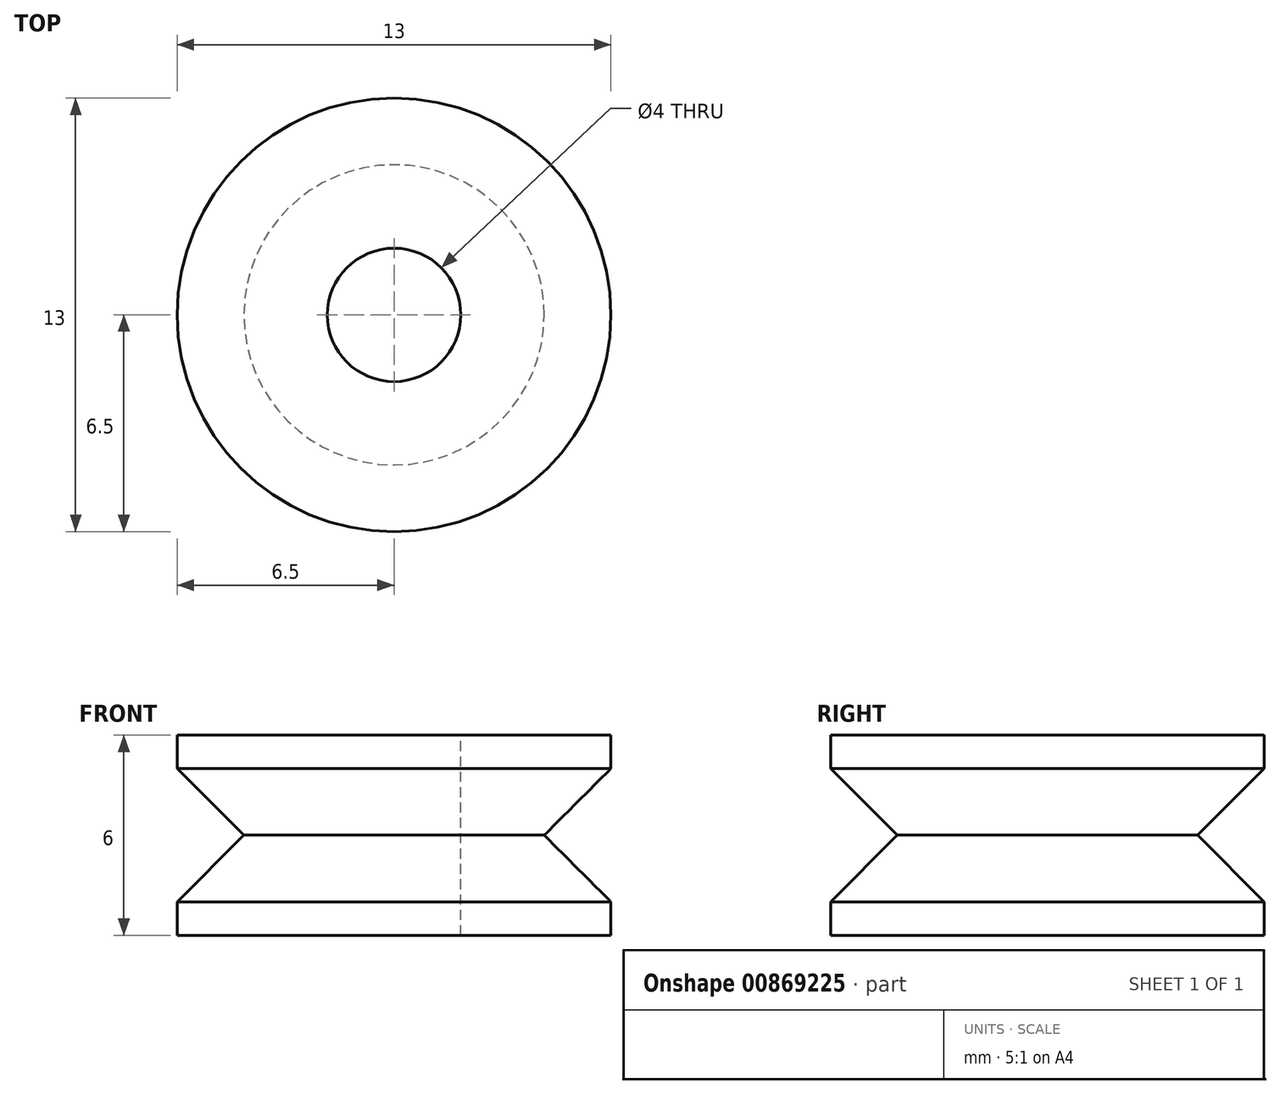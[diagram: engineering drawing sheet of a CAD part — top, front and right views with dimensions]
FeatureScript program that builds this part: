
annotation { "Feature Type Name" : "Feature", "Feature Type Description" : "" }
export const myFeature = defineFeature(function(context is Context, id is Id, definition is map)
    precondition{}
    {
        {
            var Q0;
            Q0=qCreatedBy(makeId("Front.planeOp"),FACE);
            var sketch = newSketch(context, id + "F0", { "sketchPlane" : qUnion([Q0])});
            skLineSegment(sketch, "E0.bottom", {"start": v(2, 3) * mm, "end": v(6.5, 3) * mm});
            skLineSegment(sketch, "E0.top", {"start": v(2, -3) * mm, "end": v(6.5, -3) * mm});
            skLineSegment(sketch, "E0.right", {"start": v(6.5, 3) * mm, "end": v(6.5, 2) * mm});
            skLineSegment(sketch, "E1", {"start": v(6.5, 2) * mm, "end": v(4.5, 0) * mm});
            skLineSegment(sketch, "E2", {"start": v(4.5, 0) * mm, "end": v(6.5, -2) * mm});
            skLineSegment(sketch, "E3.trimOffspring", {"start": v(6.5, -2) * mm, "end": v(6.5, -3) * mm});
            skLineSegment(sketch, "E4", {"start": v(2, 3) * mm, "end": v(2, -3) * mm});
            skPoint(sketch, "E0.left.start.orphan", {"position": v(0, 3) * mm});
            skPoint(sketch, "E5.orphan", {"position": v(0, -3) * mm});
            skLineSegment(sketch, "E6", {"start": v(0, 3) * mm, "end": v(0, -3) * mm, "construction": true});
            skSolve(sketch);
        }
        {
            var Q0;
            Q0=makeQuery(id+"F0.imprint","IMPRINT",FACE,{"disambiguationData":[TD([[makeQuery(id+"F0.imprint","IMPRINT",EDGE,{"derivedFrom":sQuery(id+"F0.wireOp",EDGE,"E0.bottom")}),-1.0]])]});
            var Q1;
            Q1=sQuery(id+"F0.wireOp",EDGE,"E6");
            revolve(context, id + "F1", {"surfaceOperationType" : NewSurfaceOperationType.NEW, "entities" : qUnion([Q0]), "axis" : qUnion([Q1]), "revolveType" : RevolveType.FULL});
        }
    });
